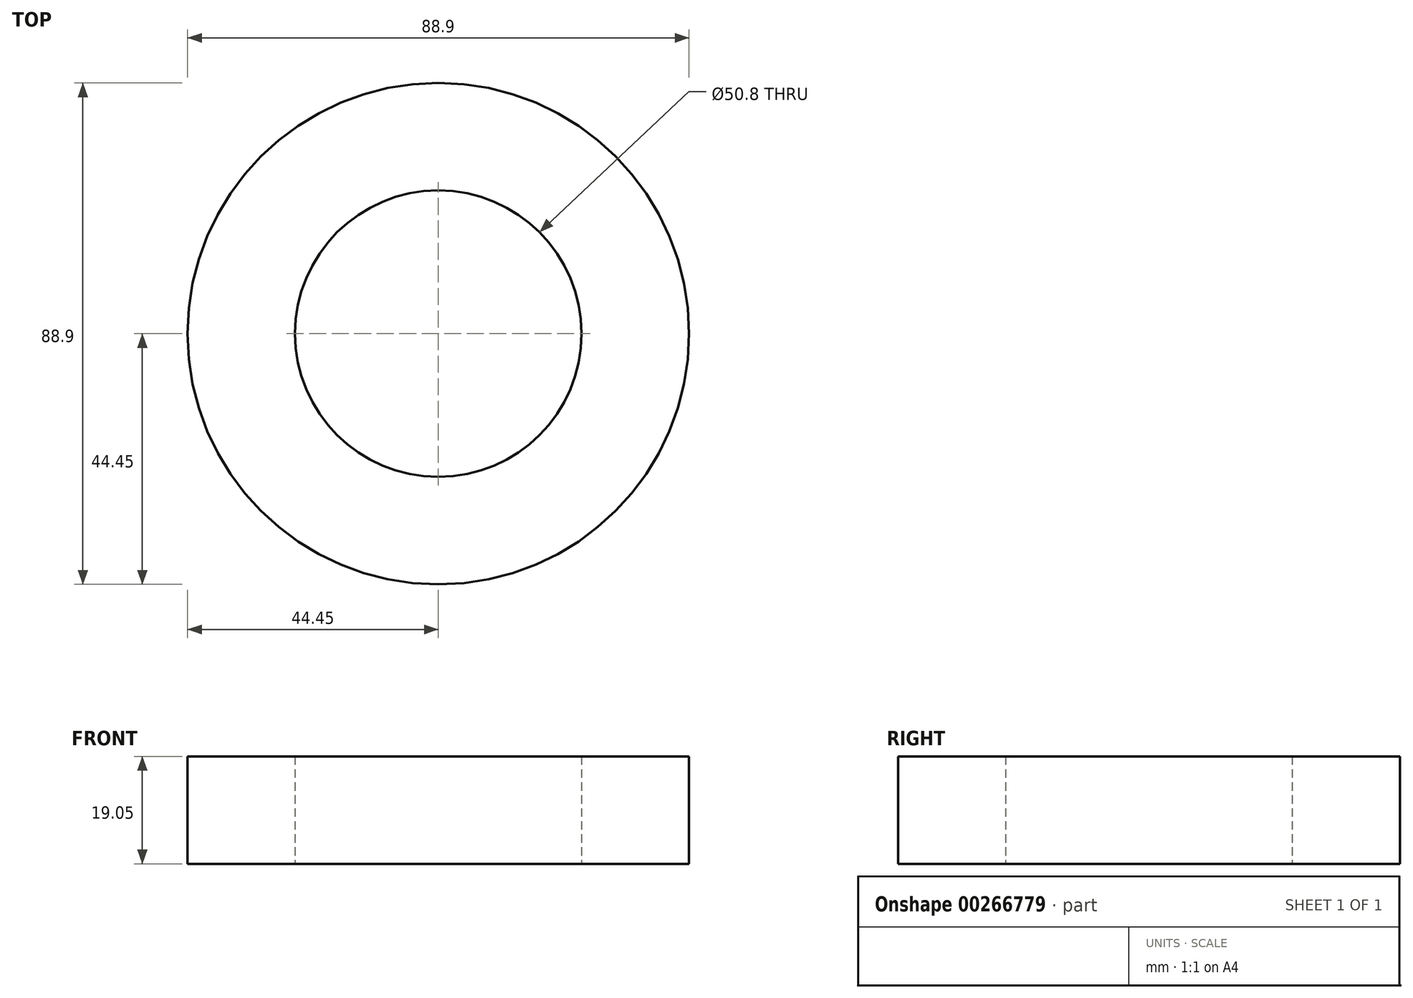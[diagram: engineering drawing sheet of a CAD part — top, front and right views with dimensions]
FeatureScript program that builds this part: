
annotation { "Feature Type Name" : "Feature", "Feature Type Description" : "" }
export const myFeature = defineFeature(function(context is Context, id is Id, definition is map)
    precondition{}
    {
        {
            var Q0;
            Q0=qCreatedBy(makeId("Top.planeOp"),FACE);
            var sketch = newSketch(context, id + "F0", { "sketchPlane" : qUnion([Q0])});
            skCircle(sketch, "E0", {"center": v(0, 0) * mm, "radius": 44.45 * mm});
            skCircle(sketch, "E1", {"center": v(0, 0) * mm, "radius": 25.4 * mm});
            skCircle(sketch, "E2", {"center": v(0, 0) * mm, "radius": 19.05 * mm});
            skSolve(sketch);
        }
        {
            var Q0;
            Q0 = qSketchRegion(id + "F0", true);
            extrude(context, id + "F1", {"entities" : qUnion([Q0]), "depth" : 19.05 * mm});
        }
    });
